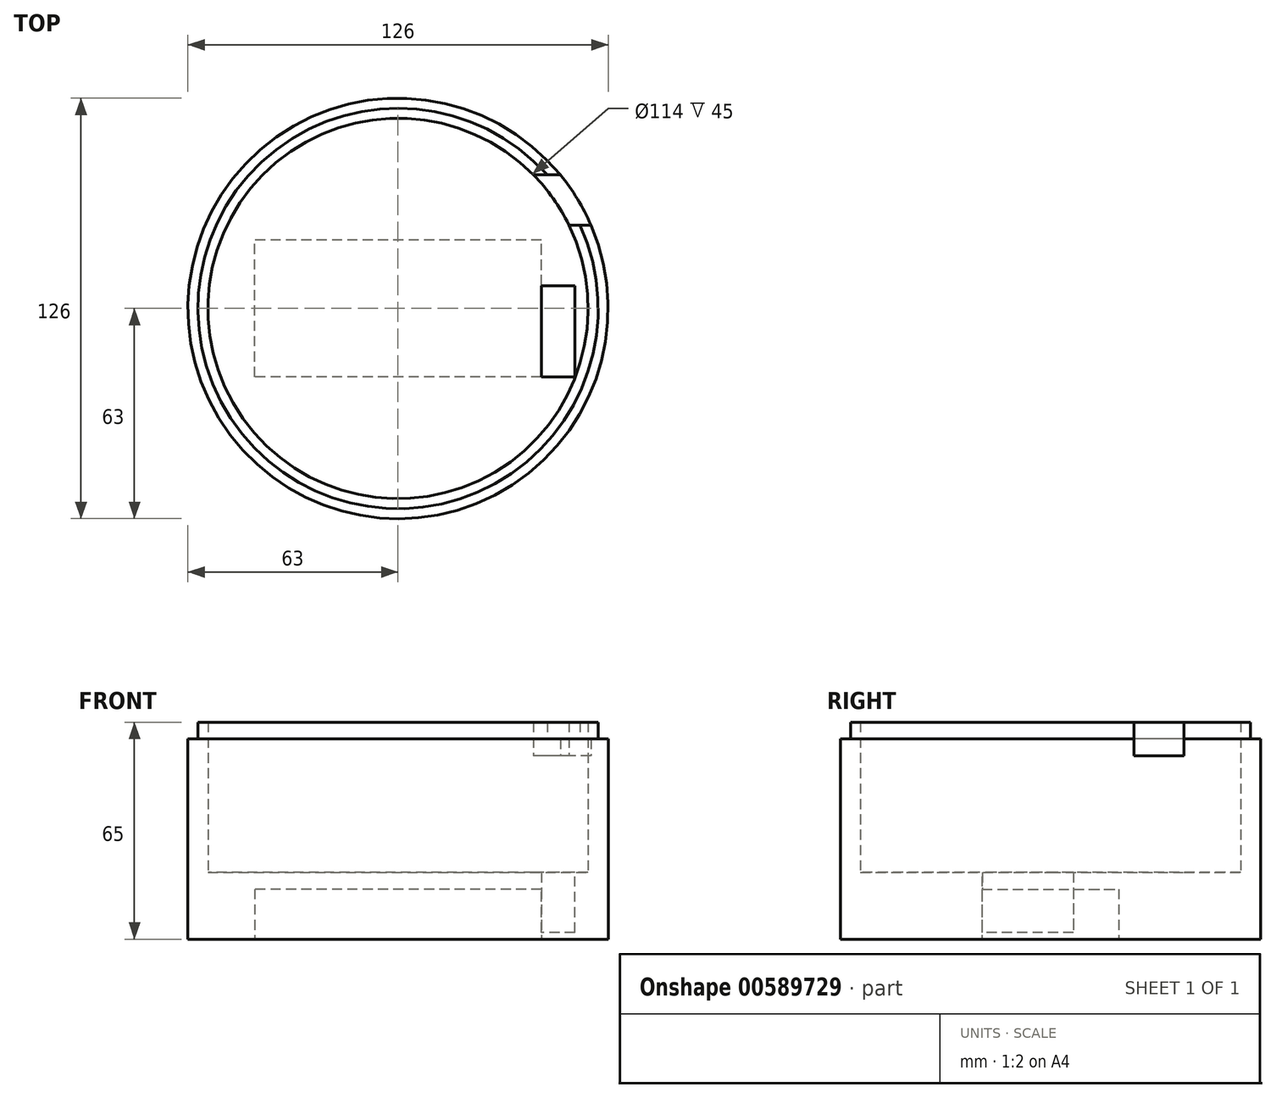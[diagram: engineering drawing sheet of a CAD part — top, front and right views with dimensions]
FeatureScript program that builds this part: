
annotation { "Feature Type Name" : "Feature", "Feature Type Description" : "" }
export const myFeature = defineFeature(function(context is Context, id is Id, definition is map)
    precondition{}
    {
        {
            var Q0;
            Q0=qCreatedBy(makeId("Top.planeOp"),FACE);
            var sketch = newSketch(context, id + "F0", { "sketchPlane" : qUnion([Q0])});
            skCircle(sketch, "E0", {"center": v(0, 0) * mm, "radius": 63 * mm});
            skCircle(sketch, "E1", {"center": v(0, 0) * mm, "radius": 60 * mm});
            skSolve(sketch);
        }
        {
            var Q0;
            Q0=qCreatedBy(makeId("Top.planeOp"),FACE);
            var sketch = newSketch(context, id + "F1", { "sketchPlane" : qUnion([Q0])});
            skCircle(sketch, "E2", {"center": v(0, 0) * mm, "radius": 57 * mm});
            skCircle(sketch, "E3", {"center": v(0, 0) * mm, "radius": 60 * mm});
            skSolve(sketch);
        }
        {
            var Q0;
            Q0=makeQuery(id+"F0.imprint","IMPRINT",FACE,{"disambiguationData":[TD([[makeQuery(id+"F0.imprint","IMPRINT",EDGE,{"derivedFrom":sQuery(id+"F0.wireOp",EDGE,"E0")}),1.0]])]});
            extrude(context, id + "F2", {"entities" : qUnion([Q0]), "depth" : 60 * mm, "offsetDistance" : 25 * mm});
        }
        {
            var Q0;
            Q0 = qSketchRegion(id + "F1", true);
            extrude(context, id + "F3", {"entities" : qUnion([Q0]), "operationType" : NewBodyOperationType.ADD, "depth" : 65 * mm, "offsetDistance" : 25 * mm});
        }
        {
            var Q0;
            Q0=qCreatedBy(makeId("Top.planeOp"),FACE);
            var sketch = newSketch(context, id + "F4", { "sketchPlane" : qUnion([Q0])});
            skCircle(sketch, "E4", {"center": v(0, 0) * mm, "radius": 57 * mm});
            skSolve(sketch);
        }
        {
            var Q0;
            Q0 = qSketchRegion(id + "F4", true);
            var Q1;
            Q1 = qSketchRegion(id + "F7", true);
            extrude(context, id + "F5", {"entities" : qUnion([Q0, Q1]), "operationType" : NewBodyOperationType.ADD, "depth" : 60 * mm, "offsetDistance" : 25 * mm});
        }
        {
            var Q0;
            Q0=qCreatedBy(makeId("Top.planeOp"),FACE);
            cPlane(context, id + "F6", {"entities" : qUnion([Q0]), "cplaneType" : CPlaneType.OFFSET, "offset" : 45 * mm, "width" : 150 * mm, "height" : 150 * mm});
        }
        {
            var Q0;
            Q0=qCreatedBy(id+"F6.planeOp",FACE);
            var sketch = newSketch(context, id + "F7", { "sketchPlane" : qUnion([Q0])});
            skCircle(sketch, "E5", {"center": v(0, 0) * mm, "radius": 57 * mm});
            skSolve(sketch);
        }
        {
            var Q0;
            Q0 = qSketchRegion(id + "F7", true);
            extrude(context, id + "F8", {"entities" : qUnion([Q0]), "operationType" : NewBodyOperationType.REMOVE, "oppositeDirection" : true, "depth" : 40 * mm, "offsetDistance" : 25 * mm});
        }
        {
            var Q0;
            Q0=qCreatedBy(makeId("Right.planeOp"),FACE);
            var sketch = newSketch(context, id + "F9", { "sketchPlane" : qUnion([Q0])});
            skLineSegment(sketch, "E6", {"start": v(0, 0) * mm, "end": v(25, 0) * mm, "construction": true});
            skLineSegment(sketch, "E7", {"start": v(25, 0) * mm, "end": v(25, 65) * mm, "construction": true});
            skLineSegment(sketch, "E8.bottom", {"start": v(25, 65) * mm, "end": v(40, 65) * mm});
            skLineSegment(sketch, "E8.top", {"start": v(25, 55) * mm, "end": v(40, 55) * mm});
            skLineSegment(sketch, "E8.left", {"start": v(25, 65) * mm, "end": v(25, 55) * mm});
            skLineSegment(sketch, "E8.right", {"start": v(40, 65) * mm, "end": v(40, 55) * mm});
            skSolve(sketch);
        }
        {
            var Q0;
            Q0=makeQuery(id+"F9.imprint","IMPRINT",FACE,{"disambiguationData":[TD([[makeQuery(id+"F9.imprint","IMPRINT",EDGE,{"derivedFrom":sQuery(id+"F9.wireOp",EDGE,"E8.bottom")}),-1.0]])]});
            extrude(context, id + "F10", {"entities" : qUnion([Q0]), "operationType" : NewBodyOperationType.REMOVE, "depth" : 279.5 * mm, "offsetDistance" : 25 * mm});
        }
        {
            var Q0;
            Q0=makeQuery(id+"F1.imprint","IMPRINT",FACE,{"disambiguationData":[TD([[makeQuery(id+"F1.imprint","IMPRINT",EDGE,{"derivedFrom":sQuery(id+"F1.wireOp",EDGE,"E2")}),1.0]])]});
            extrude(context, id + "F11", {"entities" : qUnion([Q0]), "operationType" : NewBodyOperationType.REMOVE, "depth" : 71.5 * mm, "offsetDistance" : 25 * mm});
        }
        {
            var Q0;
            Q0=qCreatedBy(makeId("Top.planeOp"),FACE);
            cPlane(context, id + "F12", {"entities" : qUnion([Q0]), "cplaneType" : CPlaneType.OFFSET, "offset" : 15 * mm, "width" : 150 * mm, "height" : 150 * mm});
        }
        {
            var Q0;
            Q0=qCreatedBy(makeId("Top.planeOp"),FACE);
            var sketch = newSketch(context, id + "F13", { "sketchPlane" : qUnion([Q0])});
            skCircle(sketch, "E9", {"center": v(0, 0) * mm, "radius": 63 * mm});
            skSolve(sketch);
        }
        {
            var Q0;
            Q0 = qSketchRegion(id + "F13", true);
            extrude(context, id + "F14", {"entities" : qUnion([Q0]), "operationType" : NewBodyOperationType.ADD, "depth" : 20 * mm, "offsetDistance" : 25 * mm});
        }
        {
            var Q0;
            Q0=qCreatedBy(makeId("Top.planeOp"),FACE);
            var sketch = newSketch(context, id + "F15", { "sketchPlane" : qUnion([Q0])});
            skLineSegment(sketch, "E10.bottom", {"start": v(43, -20.5) * mm, "end": v(-43, -20.5) * mm});
            skLineSegment(sketch, "E10.top", {"start": v(43, 20.5) * mm, "end": v(-43, 20.5) * mm});
            skLineSegment(sketch, "E10.left", {"start": v(43, -20.5) * mm, "end": v(43, 20.5) * mm});
            skLineSegment(sketch, "E10.right", {"start": v(-43, -20.5) * mm, "end": v(-43, 20.5) * mm});
            skPoint(sketch, "E10.middle", {"position": v(0, 0) * mm});
            skSolve(sketch);
        }
        {
            var Q0;
            Q0=makeQuery(id+"F15.imprint","IMPRINT",FACE,{"disambiguationData":[TD([[makeQuery(id+"F15.imprint","IMPRINT",EDGE,{"derivedFrom":sQuery(id+"F15.wireOp",EDGE,"E10.bottom")}),-1.0]])]});
            extrude(context, id + "F16", {"entities" : qUnion([Q0]), "operationType" : NewBodyOperationType.REMOVE, "depth" : 15 * mm, "offsetDistance" : 25 * mm});
        }
        {
            var Q0;
            Q0=qCreatedBy(makeId("Right.planeOp"),FACE);
            var sketch = newSketch(context, id + "F17", { "sketchPlane" : qUnion([Q0])});
            skLineSegment(sketch, "E11", {"start": v(0, 0) * mm, "end": v(0, 15) * mm, "construction": true});
            skPoint(sketch, "E12", {"position": v(0, 15) * mm});
            skLineSegment(sketch, "E13", {"start": v(0, 15) * mm, "end": v(6.83, 15) * mm});
            skLineSegment(sketch, "E14", {"start": v(6.83, 15) * mm, "end": v(6.83, 2) * mm});
            skLineSegment(sketch, "E15", {"start": v(6.83, 2) * mm, "end": v(-20.47, 2) * mm});
            skLineSegment(sketch, "E16", {"start": v(-20.47, 2) * mm, "end": v(-20.47, 15) * mm});
            skLineSegment(sketch, "E17", {"start": v(-20.47, 15) * mm, "end": v(0, 15) * mm});
            skSolve(sketch);
        }
        {
            var Q0;
            Q0 = qSketchRegion(id + "F17", true);
            extrude(context, id + "F18", {"entities" : qUnion([Q0]), "operationType" : NewBodyOperationType.REMOVE, "depth" : 53 * mm, "offsetDistance" : 25 * mm});
        }
        {
            var Q0;
            Q0=qCreatedBy(id+"F12.planeOp",FACE);
            var sketch = newSketch(context, id + "F19", { "sketchPlane" : qUnion([Q0])});
            skLineSegment(sketch, "E18", {"start": v(0, 0) * mm, "end": v(43, 0) * mm, "construction": true});
            skLineSegment(sketch, "E19", {"start": v(43, 0) * mm, "end": v(43, 6.83) * mm});
            skLineSegment(sketch, "E20", {"start": v(43, 6.83) * mm, "end": v(53, 6.83) * mm});
            skLineSegment(sketch, "E21", {"start": v(53, 6.83) * mm, "end": v(53, -20.47) * mm});
            skLineSegment(sketch, "E22", {"start": v(53, -20.47) * mm, "end": v(43, -20.47) * mm});
            skLineSegment(sketch, "E23", {"start": v(43, -20.47) * mm, "end": v(43, 6.83) * mm});
            skSolve(sketch);
        }
        {
            var Q0;
            Q0 = qSketchRegion(id + "F19", true);
            extrude(context, id + "F20", {"entities" : qUnion([Q0]), "operationType" : NewBodyOperationType.REMOVE, "depth" : 128 * mm, "offsetDistance" : 25 * mm});
        }
    });
